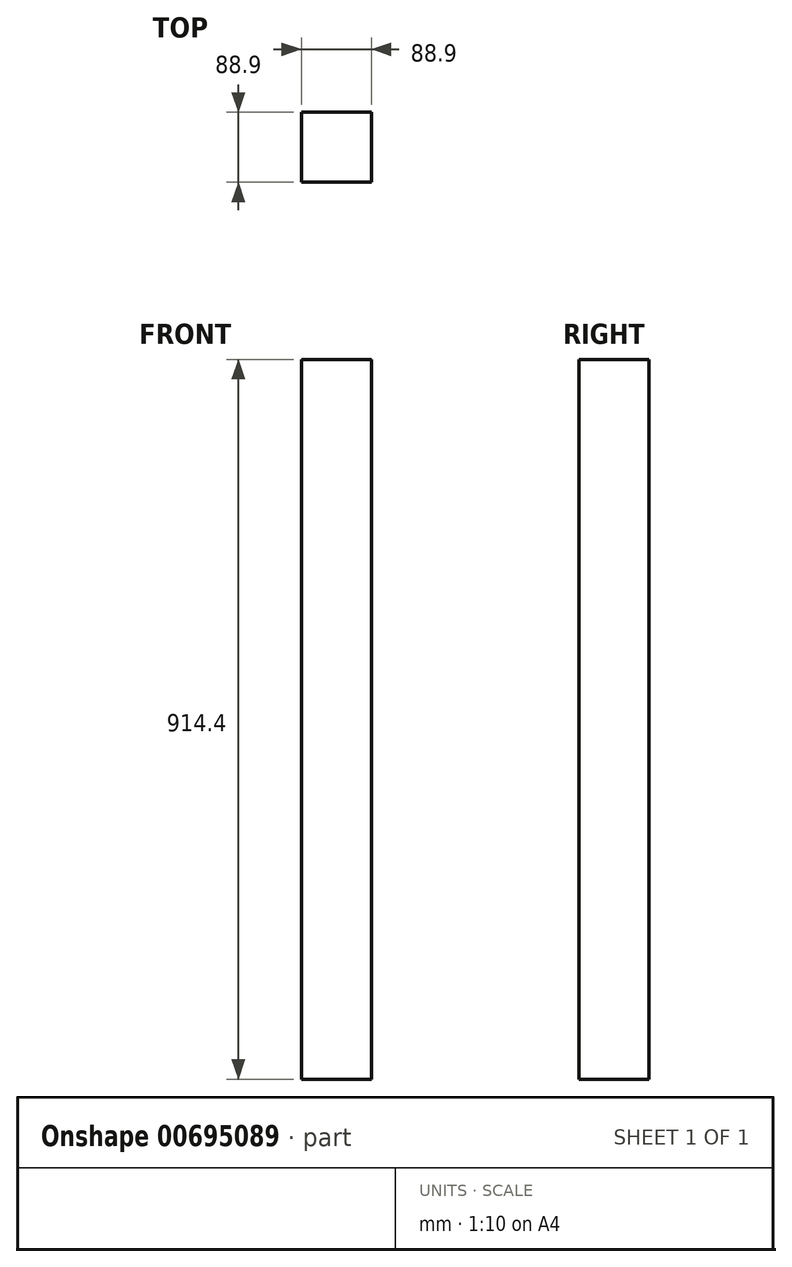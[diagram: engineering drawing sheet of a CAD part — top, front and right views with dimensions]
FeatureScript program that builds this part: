
annotation { "Feature Type Name" : "Feature", "Feature Type Description" : "" }
export const myFeature = defineFeature(function(context is Context, id is Id, definition is map)
    precondition{}
    {
        {
            var Q0;
            Q0=qCreatedBy(makeId("Top.planeOp"),FACE);
            var sketch = newSketch(context, id + "F0", { "sketchPlane" : qUnion([Q0])});
            skLineSegment(sketch, "E0.bottom", {"start": v(0, 0) * mm, "end": v(88.9, 0) * mm});
            skLineSegment(sketch, "E0.top", {"start": v(0, 88.9) * mm, "end": v(88.9, 88.9) * mm});
            skLineSegment(sketch, "E0.left", {"start": v(0, 0) * mm, "end": v(0, 88.9) * mm});
            skLineSegment(sketch, "E0.right", {"start": v(88.9, 0) * mm, "end": v(88.9, 88.9) * mm});
            skSolve(sketch);
        }
        {
            var Q0;
            Q0 = qSketchRegion(id + "F0", true);
            extrude(context, id + "F1", {"entities" : qUnion([Q0]), "depth" : 914.4 * mm, "offsetDistance" : 25.4 * mm});
        }
    });
